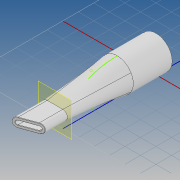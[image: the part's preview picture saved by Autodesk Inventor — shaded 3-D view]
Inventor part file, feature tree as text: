
AUTODESK INVENTOR PART (.ipt)
format: ipt  version: 2021 (Build 250183000, 183)  size: 306,688 bytes
history: native  units: mm
features: sketch x5, projected_geometry x5, extrude x4, other x4, loft x2, plane x1, fillet x1
ambient origin geometry x8: Origin, YZ Plane, XZ Plane, XY Plane, X Axis, Y Axis, Z Axis, Center Point
bodies: Solid1 (feature_tree), Solid3 (feature_tree)
feature tree (22):
  extrude  "Extrusion1"  Depth=80.0mm
  plane  "Work Plane1"
  sketch  "Sketch3"  dims[d5=10.0mm d6=12.0mm]
  extrude  "Extrusion2"  Depth=12.0mm
  sketch  "Sketch7"  dims[d19=3.5mm d22=41.65mm]
  extrude  "Extrusion5"  Depth=50.0mm TaperAngle=0.0deg
  loft  "Loft3"
  loft  "Loft5"
  extrude  "Extrusion6"  TaperAngle=0.0deg  [1 undecoded]
  fillet  "Fillet1"  [1 undecoded]
  sketch  "Sketch2"  dims[d2=50.0mm d3=0.0mm d4=80.0mm]
  projected_geometry  "Projected Loop1"
  sketch  "Sketch4"  dims[d11=34.65mm d12=50.0mm d13=0.0mm]
  projected_geometry  "Projected Loop5"
  other  "Edges4"
  other  "Edges5"
  other  "Edges8"
  other  "Edges9"
  sketch  "Sketch8"  dims[d23=40.0mm d24=0.0mm d33=0.0mm d34=90.0deg d35=0.0mm d36=90.0deg d41=0.0mm d42=90.0deg d43=0.0mm d44=90.0deg d45=3.490659mm d46=10.0mm d47=0.0mm d48=0.5mm]
  projected_geometry  "Projected Loop7"
  projected_geometry  "Projected Loop8"
  projected_geometry  "Projected Loop9"
note: 2 required parameter values undecoded (feature->parameter linkage not recoverable at this tier; creation-order binding heuristic only, values carry confidence <= 0.55)
